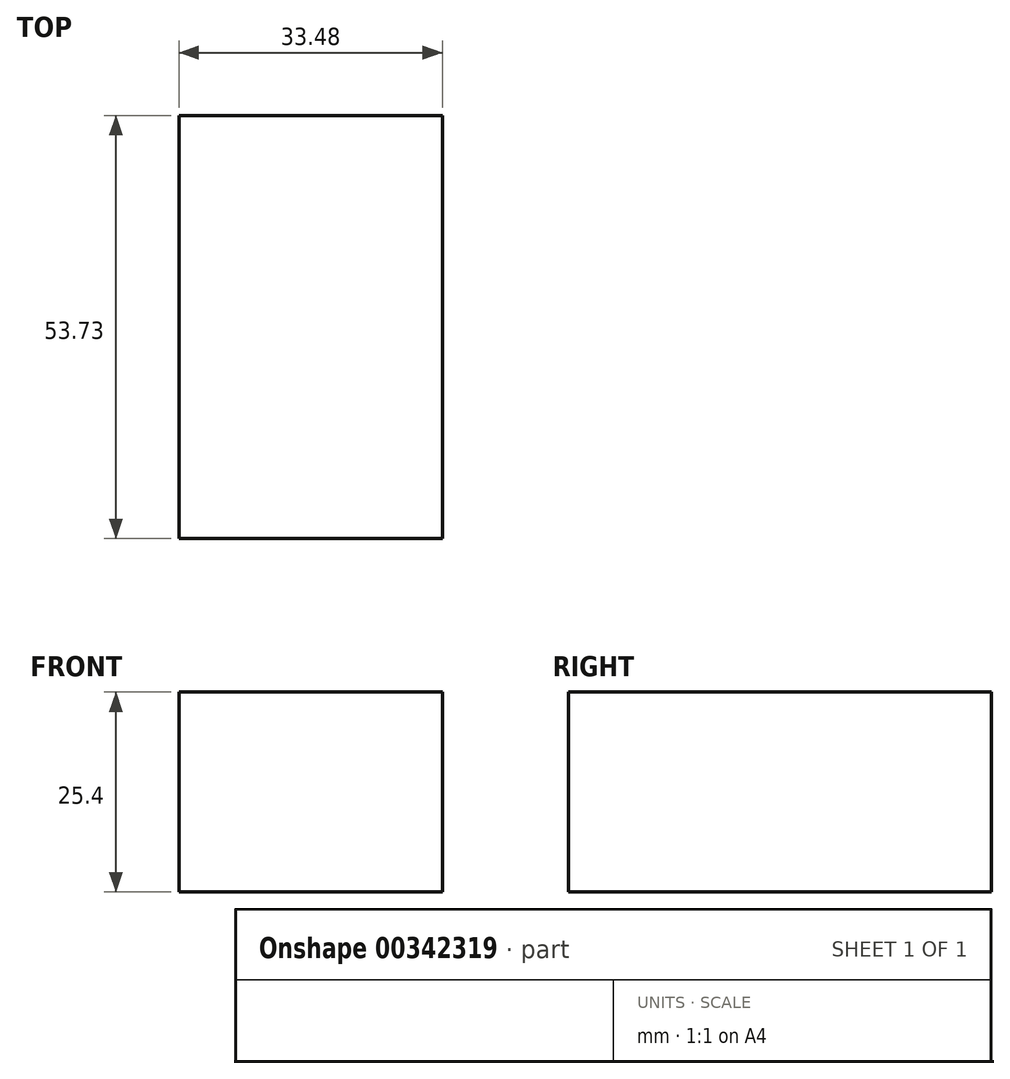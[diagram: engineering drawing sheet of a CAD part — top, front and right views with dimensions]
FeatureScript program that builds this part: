
annotation { "Feature Type Name" : "Feature", "Feature Type Description" : "" }
export const myFeature = defineFeature(function(context is Context, id is Id, definition is map)
    precondition{}
    {
        {
            var Q0;
            Q0=qCreatedBy(makeId("Top.planeOp"),FACE);
            var sketch = newSketch(context, id + "F0", { "sketchPlane" : qUnion([Q0])});
            skLineSegment(sketch, "E0.bottom", {"start": v(0, 0) * mm, "end": v(33.48, 0) * mm});
            skLineSegment(sketch, "E0.top", {"start": v(0, 53.73) * mm, "end": v(33.48, 53.73) * mm});
            skLineSegment(sketch, "E0.left", {"start": v(0, 0) * mm, "end": v(0, 53.73) * mm});
            skLineSegment(sketch, "E0.right", {"start": v(33.48, 0) * mm, "end": v(33.48, 53.73) * mm});
            skSolve(sketch);
        }
        {
            var Q0;
            Q0 = qSketchRegion(id + "F0", true);
            extrude(context, id + "F1", {"entities" : qUnion([Q0]), "depth" : 25.4 * mm});
        }
    });
